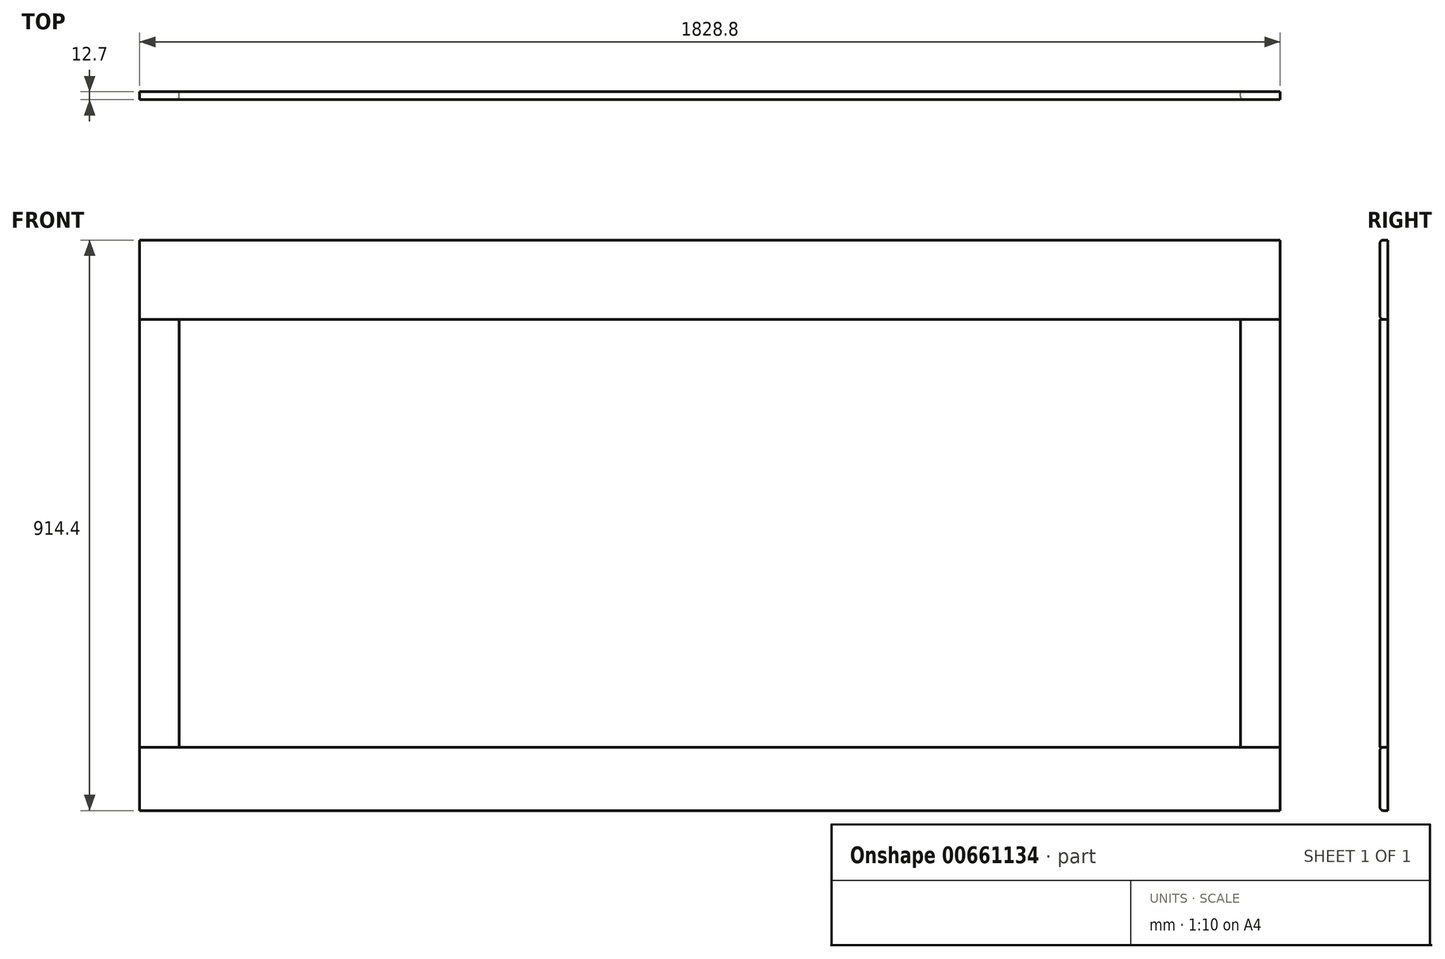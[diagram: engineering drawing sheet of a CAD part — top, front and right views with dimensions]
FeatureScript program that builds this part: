
annotation { "Feature Type Name" : "Feature", "Feature Type Description" : "" }
export const myFeature = defineFeature(function(context is Context, id is Id, definition is map)
    precondition{}
    {
        {
            var Q0;
            Q0=qCreatedBy(makeId("Front.planeOp"),FACE);
            var sketch = newSketch(context, id + "F0", { "sketchPlane" : qUnion([Q0])});
            skLineSegment(sketch, "E0.bottom", {"start": v(914.4, -457.2) * mm, "end": v(-914.4, -457.2) * mm});
            skLineSegment(sketch, "E0.top", {"start": v(914.4, 457.2) * mm, "end": v(-914.4, 457.2) * mm});
            skLineSegment(sketch, "E0.left", {"start": v(914.4, -457.2) * mm, "end": v(914.4, 457.2) * mm});
            skLineSegment(sketch, "E0.right", {"start": v(-914.4, -457.2) * mm, "end": v(-914.4, 457.2) * mm});
            skPoint(sketch, "E0.middle", {"position": v(0, 0) * mm});
            skLineSegment(sketch, "E1", {"start": v(0, 457.2) * mm, "end": v(0, -457.2) * mm, "construction": true});
            skLineSegment(sketch, "E2.0", {"start": v(914.4, 330.2) * mm, "end": v(-914.4, 330.2) * mm});
            skLineSegment(sketch, "E3.0", {"start": v(914.4, -355.6) * mm, "end": v(-914.4, -355.6) * mm});
            skLineSegment(sketch, "E4", {"start": v(-850.9, 330.2) * mm, "end": v(-850.9, -355.6) * mm});
            skLineSegment(sketch, "E5", {"start": v(850.9, 330.2) * mm, "end": v(850.9, -355.6) * mm});
            skLineSegment(sketch, "E6.bottom", {"start": v(-31.75, 330.2) * mm, "end": v(31.75, 330.2) * mm});
            skLineSegment(sketch, "E6.top", {"start": v(-31.75, -355.6) * mm, "end": v(31.75, -355.6) * mm});
            skLineSegment(sketch, "E6.left", {"start": v(-31.75, 330.2) * mm, "end": v(-31.75, -355.6) * mm});
            skLineSegment(sketch, "E6.right", {"start": v(31.75, 330.2) * mm, "end": v(31.75, -355.6) * mm});
            skLineSegment(sketch, "E7", {"start": v(0, 330.2) * mm, "end": v(0, 457.2) * mm});
            skSolve(sketch);
        }
        {
            var Q0;
            {var subQ8=sQuery(id+"F0.wireOp",EDGE,"E7");Q0=makeQuery(id+"F0.imprint","IMPRINT",FACE,{"disambiguationData":[TD([[makeQuery(id+"F0.imprint","IMPRINT",EDGE,{"derivedFrom":subQ8}),1.0]])]});}
            var Q1;
            {var subQ6=sQuery(id+"F0.wireOp",EDGE,"E7");Q1=makeQuery(id+"F0.imprint","IMPRINT",FACE,{"disambiguationData":[TD([[makeQuery(id+"F0.imprint","IMPRINT",EDGE,{"derivedFrom":subQ6}),-1.0]])]});}
            var Q2;
            {var subQ1=sQuery(id+"F0.wireOp",EDGE,"E0.bottom");Q2=makeQuery(id+"F0.imprint","IMPRINT",FACE,{"disambiguationData":[TD([[makeQuery(id+"F0.imprint","IMPRINT",EDGE,{"derivedFrom":subQ1}),-1.0]])]});}
            extrude(context, id + "F1", {"entities" : qUnion([Q0, Q1, Q2]), "depth" : 12.7 * mm, "offsetDistance" : 25.4 * mm});
        }
        {
            var Q0;
            {var subQ5=sQuery(id+"F0.wireOp",EDGE,"E4");Q0=makeQuery(id+"F0.imprint","IMPRINT",FACE,{"disambiguationData":[TD([[makeQuery(id+"F0.imprint","IMPRINT",EDGE,{"derivedFrom":subQ5}),-1.0]])]});}
            var Q1;
            Q1=makeQuery(id+"F0.imprint","IMPRINT",FACE,{"disambiguationData":[TD([[makeQuery(id+"F0.imprint","IMPRINT",EDGE,{"derivedFrom":sQuery(id+"F0.wireOp",EDGE,"E6.top")}),1.0]])]});
            var Q2;
            {var subQ5=sQuery(id+"F0.wireOp",EDGE,"E5");Q2=makeQuery(id+"F0.imprint","IMPRINT",FACE,{"disambiguationData":[TD([[makeQuery(id+"F0.imprint","IMPRINT",EDGE,{"derivedFrom":subQ5}),1.0]])]});}
            extrude(context, id + "F2", {"entities" : qUnion([Q0, Q1, Q2]), "depth" : 12.7 * mm, "offsetDistance" : 25.4 * mm});
        }
        {
            var Q0;
            Q0=makeQuery(id+"F1.opExtrude","CAP_EDGE",EDGE,{"disambiguationData":[OSD([sQuery(id+"F0.wireOp",EDGE,"E0.top")])],"isStart":false});
            var Q1;
            Q1=makeQuery(id+"F1.opExtrude","CAP_EDGE",EDGE,{"disambiguationData":[OSD([sQuery(id+"F0.wireOp",EDGE,"E2.0"),sQuery(id+"F0.wireOp",EDGE,"E6.bottom")])],"isStart":false});
            var Q2;
            Q2=makeQuery(id+"F2.opExtrude","CAP_EDGE",EDGE,{"disambiguationData":[OSD([sQuery(id+"F0.wireOp",EDGE,"E0.left")])],"isStart":false});
            var Q3;
            Q3=makeQuery(id+"F2.opExtrude","CAP_EDGE",EDGE,{"disambiguationData":[OSD([sQuery(id+"F0.wireOp",EDGE,"E5")])],"isStart":false});
            var Q4;
            Q4=makeQuery(id+"F2.opExtrude","CAP_EDGE",EDGE,{"disambiguationData":[OSD([sQuery(id+"F0.wireOp",EDGE,"E4")])],"isStart":false});
            var Q5;
            Q5=makeQuery(id+"F2.opExtrude","CAP_EDGE",EDGE,{"disambiguationData":[OSD([sQuery(id+"F0.wireOp",EDGE,"E0.right")])],"isStart":false});
            var Q6;
            Q6=makeQuery(id+"F2.opExtrude","CAP_EDGE",EDGE,{"disambiguationData":[OSD([sQuery(id+"F0.wireOp",EDGE,"E6.left")])],"isStart":false});
            var Q7;
            Q7=makeQuery(id+"F2.opExtrude","CAP_EDGE",EDGE,{"disambiguationData":[OSD([sQuery(id+"F0.wireOp",EDGE,"E6.right")])],"isStart":false});
            var Q8;
            Q8=makeQuery(id+"F1.opExtrude","CAP_EDGE",EDGE,{"disambiguationData":[OSD([sQuery(id+"F0.wireOp",EDGE,"E3.0"),sQuery(id+"F0.wireOp",EDGE,"E6.top")])],"isStart":false});
            var Q9;
            Q9=makeQuery(id+"F1.opExtrude","CAP_EDGE",EDGE,{"disambiguationData":[OSD([sQuery(id+"F0.wireOp",EDGE,"E0.bottom")])],"isStart":false});
            fillet(context, id + "F3", {"entities" : qUnion([Q0, Q1, Q2, Q3, Q4, Q5, Q6, Q7, Q8, Q9]), "radius" : 5.08 * mm, "tangentPropagation" : true, "allowEdgeOverflow" : false});
        }
    });
